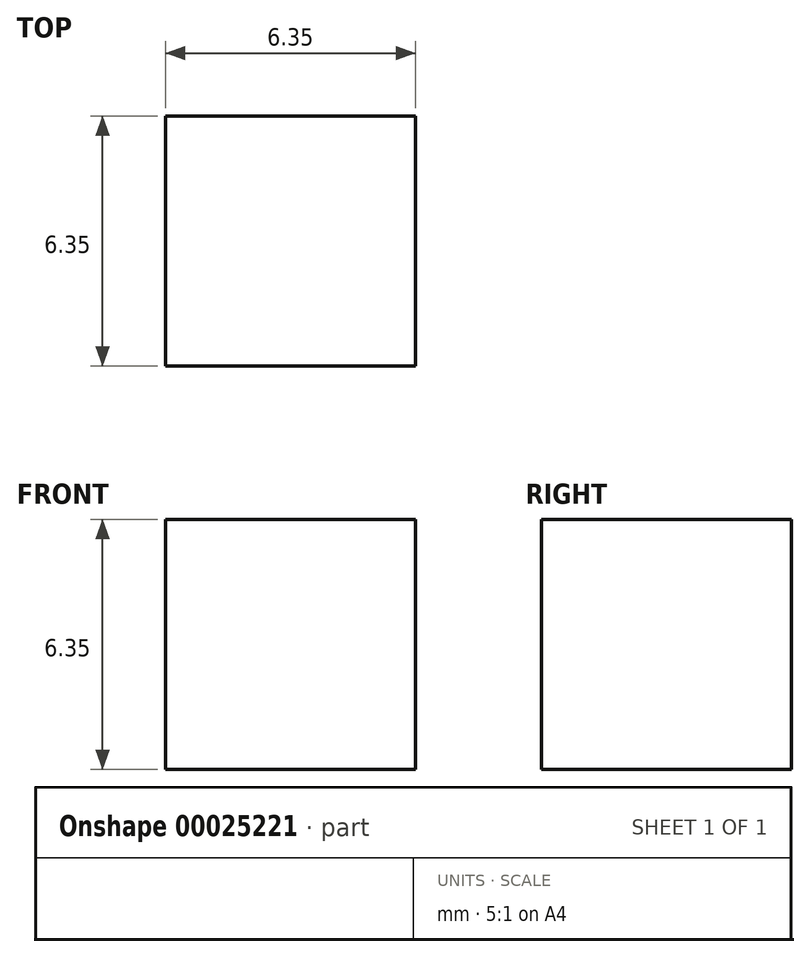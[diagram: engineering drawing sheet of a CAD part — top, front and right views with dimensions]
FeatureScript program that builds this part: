
annotation { "Feature Type Name" : "Feature", "Feature Type Description" : "" }
export const myFeature = defineFeature(function(context is Context, id is Id, definition is map)
    precondition{}
    {
        {
            var Q0;
            Q0=qCreatedBy(makeId("Front.planeOp"),FACE);
            var sketch = newSketch(context, id + "F0", { "sketchPlane" : qUnion([Q0])});
            skLineSegment(sketch, "E0.bottom", {"start": v(0, 0) * mm, "end": v(6.35, 0) * mm});
            skLineSegment(sketch, "E0.top", {"start": v(0, 6.35) * mm, "end": v(6.35, 6.35) * mm});
            skLineSegment(sketch, "E0.left", {"start": v(0, 0) * mm, "end": v(0, 6.35) * mm});
            skLineSegment(sketch, "E0.right", {"start": v(6.35, 0) * mm, "end": v(6.35, 6.35) * mm});
            skSolve(sketch);
        }
        {
            var Q0;
            Q0 = qSketchRegion(id + "F0", true);
            extrude(context, id + "F1", {"entities" : qUnion([Q0]), "depth" : 6.35 * mm});
        }
    });
